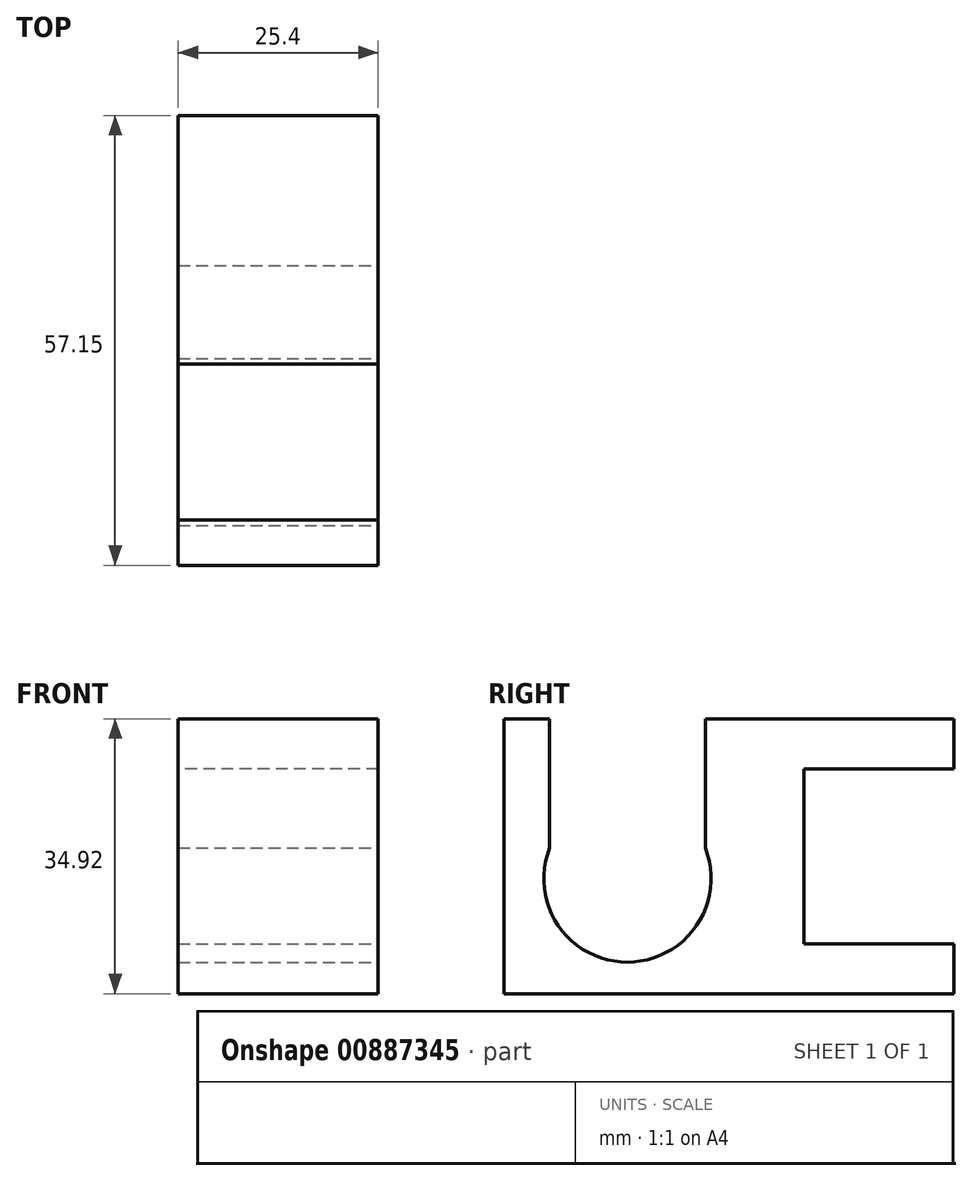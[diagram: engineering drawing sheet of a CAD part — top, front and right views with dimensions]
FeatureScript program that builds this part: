
annotation { "Feature Type Name" : "Feature", "Feature Type Description" : "" }
export const myFeature = defineFeature(function(context is Context, id is Id, definition is map)
    precondition{}
    {
        {
            var Q0;
            Q0=qCreatedBy(makeId("Top.planeOp"),FACE);
            var sketch = newSketch(context, id + "F0", { "sketchPlane" : qUnion([Q0])});
            skLineSegment(sketch, "E0.bottom", {"start": v(0, 8.28) * mm, "end": v(-25.4, 8.28) * mm});
            skLineSegment(sketch, "E0.top", {"start": v(0, -23.47) * mm, "end": v(-25.4, -23.47) * mm});
            skLineSegment(sketch, "E0.left", {"start": v(0, 8.28) * mm, "end": v(0, -23.47) * mm});
            skLineSegment(sketch, "E0.right", {"start": v(-25.4, 8.28) * mm, "end": v(-25.4, -23.47) * mm});
            skSolve(sketch);
        }
        {
            var Q0;
            Q0=makeQuery(id+"F0.imprint","IMPRINT",FACE,{"disambiguationData":[TD([[makeQuery(id+"F0.imprint","IMPRINT",EDGE,{"derivedFrom":sQuery(id+"F0.wireOp",EDGE,"E0.bottom")}),1.0]])]});
            var sketch = newSketch(context, id + "F1", { "sketchPlane" : qUnion([Q0])});
            skLineSegment(sketch, "E1.bottom", {"start": v(0, -23.47) * mm, "end": v(-25.4, -23.47) * mm});
            skLineSegment(sketch, "E1.top", {"start": v(0, -10.77) * mm, "end": v(-25.4, -10.77) * mm});
            skLineSegment(sketch, "E1.left", {"start": v(0, -23.47) * mm, "end": v(0, -10.77) * mm});
            skLineSegment(sketch, "E1.right", {"start": v(-25.4, -23.47) * mm, "end": v(-25.4, -10.77) * mm});
            skSolve(sketch);
        }
        {
            var Q0;
            Q0=makeQuery(id+"F0.imprint","IMPRINT",FACE,{"disambiguationData":[TD([[makeQuery(id+"F0.imprint","IMPRINT",EDGE,{"derivedFrom":sQuery(id+"F0.wireOp",EDGE,"E0.bottom")}),1.0]])]});
            extrude(context, id + "F2", {"entities" : qUnion([Q0]), "depth" : 6.35 * mm, "offsetDistance" : 25.4 * mm});
        }
        {
            var Q0;
            Q0 = qSketchRegion(id + "F1", true);
            extrude(context, id + "F3", {"entities" : qUnion([Q0]), "operationType" : NewBodyOperationType.ADD, "depth" : 28.57 * mm, "offsetDistance" : 25.4 * mm});
        }
        {
            var Q0;
            Q0=makeQuery(id+"F3.opExtrude","CAP_FACE",FACE,{"disambiguationData":[OSD([sQuery(id+"F1.wireOp",EDGE,"E1.bottom"),sQuery(id+"F1.wireOp",EDGE,"E1.top"),sQuery(id+"F1.wireOp",EDGE,"E1.left"),sQuery(id+"F1.wireOp",EDGE,"E1.right")])],"isStart":false});
            var sketch = newSketch(context, id + "F4", { "sketchPlane" : qUnion([Q0])});
            skLineSegment(sketch, "E2.bottom", {"start": v(0, -23.47) * mm, "end": v(-25.4, -23.47) * mm});
            skLineSegment(sketch, "E2.top", {"start": v(0, 8.28) * mm, "end": v(-25.4, 8.28) * mm});
            skLineSegment(sketch, "E2.left", {"start": v(0, -23.47) * mm, "end": v(0, 8.28) * mm});
            skLineSegment(sketch, "E2.right", {"start": v(-25.4, -23.47) * mm, "end": v(-25.4, 8.28) * mm});
            skSolve(sketch);
        }
        {
            var Q0;
            Q0 = qSketchRegion(id + "F4", true);
            extrude(context, id + "F5", {"entities" : qUnion([Q0]), "operationType" : NewBodyOperationType.ADD, "depth" : 6.35 * mm, "offsetDistance" : 25.4 * mm});
        }
        {
            var Q0;
            Q0=qCreatedBy(makeId("Right.planeOp"),FACE);
            var sketch = newSketch(context, id + "F6", { "sketchPlane" : qUnion([Q0])});
            skLineSegment(sketch, "E3.bottom", {"start": v(-23.47, 0) * mm, "end": v(-48.87, 0) * mm});
            skLineSegment(sketch, "E3.top", {"start": v(-23.47, 34.93) * mm, "end": v(-48.87, 34.93) * mm});
            skLineSegment(sketch, "E3.left", {"start": v(-23.47, 0) * mm, "end": v(-23.47, 34.93) * mm});
            skLineSegment(sketch, "E3.right", {"start": v(-48.87, 0) * mm, "end": v(-48.87, 34.93) * mm});
            skSolve(sketch);
        }
        {
            var Q0;
            Q0=makeQuery(id+"F6.imprint","IMPRINT",FACE,{"disambiguationData":[TD([[makeQuery(id+"F6.imprint","IMPRINT",EDGE,{"derivedFrom":sQuery(id+"F6.wireOp",EDGE,"E3.bottom")}),-1.0]])]});
            extrude(context, id + "F7", {"entities" : qUnion([Q0]), "operationType" : NewBodyOperationType.ADD, "oppositeDirection" : true, "depth" : 25.4 * mm, "offsetDistance" : 25.4 * mm});
        }
        {
            var Q0;
            Q0=makeQuery(id+"F7.boolean.opBoolean","MERGE",FACE,{"derivedFrom":[makeQuery(id+"F5.boolean.opBoolean","MERGE",FACE,{"derivedFrom":[makeQuery(id+"F3.boolean.opBoolean","MERGE",FACE,{"derivedFrom":[makeQuery(id+"F2.opExtrude","SWEPT_FACE",FACE,{"disambiguationData":[OSD([sQuery(id+"F0.wireOp",EDGE,"E0.left")])]}),makeQuery(id+"F3.opExtrude","SWEPT_FACE",FACE,{"disambiguationData":[OSD([sQuery(id+"F1.wireOp",EDGE,"E1.left")])]})]}),makeQuery(id+"F5.opExtrude","SWEPT_FACE",FACE,{"disambiguationData":[OSD([sQuery(id+"F4.wireOp",EDGE,"E2.left")])]})]}),makeQuery(id+"F7.opExtrude","CAP_FACE",FACE,{"disambiguationData":[OSD([sQuery(id+"F6.wireOp",EDGE,"E3.bottom"),sQuery(id+"F6.wireOp",EDGE,"E3.top"),sQuery(id+"F6.wireOp",EDGE,"E3.left"),sQuery(id+"F6.wireOp",EDGE,"E3.right")])],"isStart":true})]});
            var sketch = newSketch(context, id + "F8", { "sketchPlane" : qUnion([Q0])});
            skLineSegment(sketch, "E4.bottom", {"start": v(-43.1, 34.93) * mm, "end": v(-23.3, 34.93) * mm});
            skLineSegment(sketch, "E4.top", {"start": v(-43.1, 18.49) * mm, "end": v(-23.3, 18.49) * mm});
            skLineSegment(sketch, "E4.left", {"start": v(-43.1, 34.93) * mm, "end": v(-43.1, 18.49) * mm});
            skLineSegment(sketch, "E4.right", {"start": v(-23.3, 34.93) * mm, "end": v(-23.3, 18.49) * mm});
            skArc(sketch, "E5", {"start": v(-43.1, 18.49) * mm, "mid": v(-33.2, 4) * mm, "end": v(-23.3, 18.49) * mm});
            skSolve(sketch);
        }
        {
            var Q0;
            Q0 = qSketchRegion(id + "F8", true);
            extrude(context, id + "F9", {"entities" : qUnion([Q0]), "operationType" : NewBodyOperationType.REMOVE, "oppositeDirection" : true, "depth" : 33.78 * mm, "offsetDistance" : 25.4 * mm});
        }
    });
